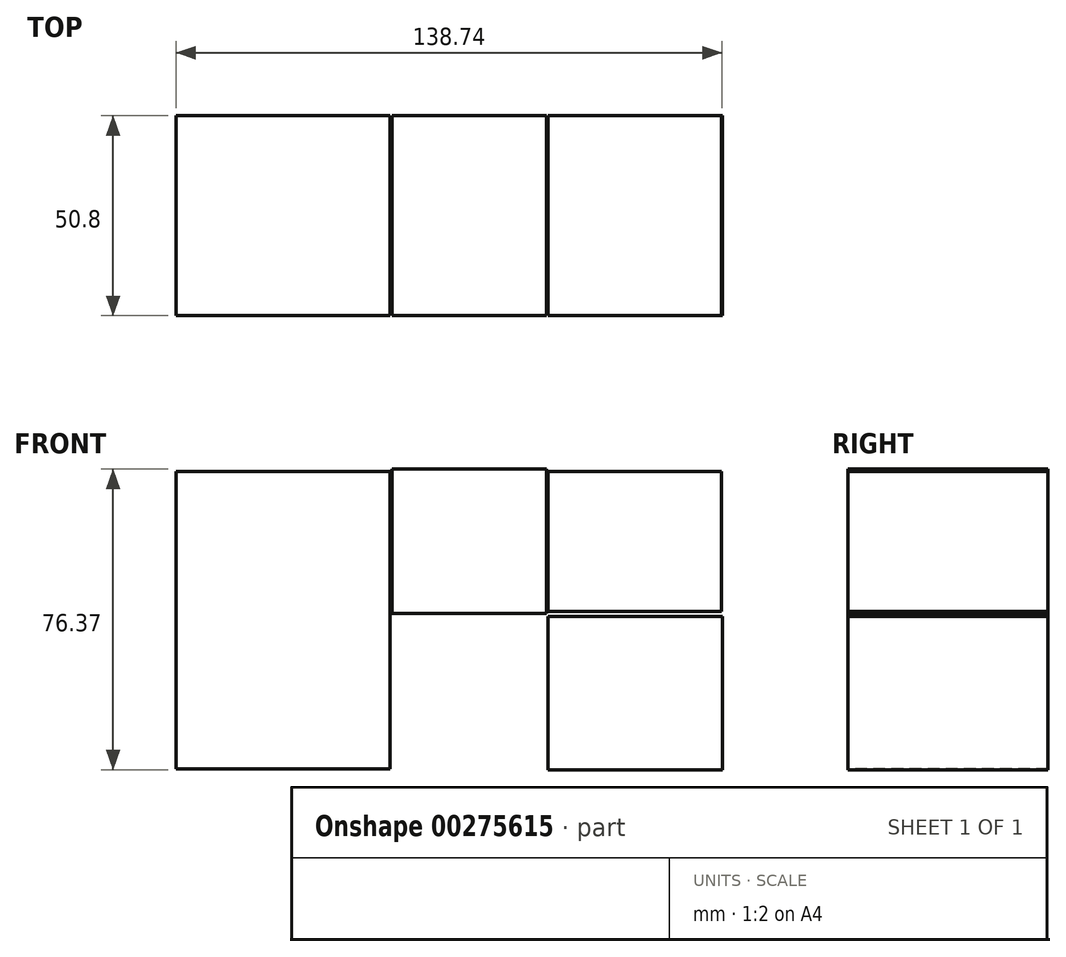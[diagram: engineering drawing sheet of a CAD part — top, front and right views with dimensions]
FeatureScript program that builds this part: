
annotation { "Feature Type Name" : "Feature", "Feature Type Description" : "" }
export const myFeature = defineFeature(function(context is Context, id is Id, definition is map)
    precondition{}
    {
        {
            var Q0;
            Q0=qCreatedBy(makeId("Front.planeOp"),FACE);
            var sketch = newSketch(context, id + "F0", { "sketchPlane" : qUnion([Q0])});
            skLineSegment(sketch, "E0.bottom", {"start": v(19.66, -0.53) * mm, "end": v(-19.66, -0.53) * mm});
            skLineSegment(sketch, "E0.top", {"start": v(19.66, 36.14) * mm, "end": v(-19.66, 36.14) * mm});
            skLineSegment(sketch, "E0.left", {"start": v(19.66, -0.53) * mm, "end": v(19.66, 36.14) * mm});
            skLineSegment(sketch, "E0.right", {"start": v(-19.66, -0.53) * mm, "end": v(-19.66, 36.14) * mm});
            skPoint(sketch, "E0.middle", {"position": v(0, 17.8) * mm});
            skLineSegment(sketch, "E1.bottom", {"start": v(64.1, 0) * mm, "end": v(20.06, 0) * mm});
            skLineSegment(sketch, "E1.top", {"start": v(64.1, 35.6) * mm, "end": v(20.06, 35.6) * mm});
            skLineSegment(sketch, "E1.left", {"start": v(64.1, 0) * mm, "end": v(64.1, 35.6) * mm});
            skLineSegment(sketch, "E1.right", {"start": v(20.06, 0) * mm, "end": v(20.06, 35.6) * mm});
            skPoint(sketch, "E1.middle", {"position": v(42.08, 17.8) * mm});
            skPoint(sketch, "E1.middle.positionSnap0", {"position": v(19.66, 17.8) * mm});
            skPoint(sketch, "E1.centerSnap0", {"position": v(19.66, 17.8) * mm});
            skLineSegment(sketch, "E2.bottom", {"start": v(-20.1, 0) * mm, "end": v(-74.46, 0) * mm});
            skLineSegment(sketch, "E2.top", {"start": v(-20.1, 35.6) * mm, "end": v(-74.46, 35.6) * mm});
            skLineSegment(sketch, "E2.left", {"start": v(-20.1, 0) * mm, "end": v(-20.1, 35.6) * mm});
            skLineSegment(sketch, "E2.right", {"start": v(-74.46, 0) * mm, "end": v(-74.46, 35.6) * mm});
            skPoint(sketch, "E2.middle", {"position": v(-47.28, 17.8) * mm});
            skLineSegment(sketch, "E3.bottom", {"start": v(-20.1, -40.04) * mm, "end": v(-74.46, -40.04) * mm});
            skLineSegment(sketch, "E3.left", {"start": v(-20.1, -40.04) * mm, "end": v(-20.1, 0) * mm});
            skLineSegment(sketch, "E3.right", {"start": v(-74.46, -40.04) * mm, "end": v(-74.46, 0) * mm});
            skPoint(sketch, "E3.middle", {"position": v(-47.28, -20.02) * mm});
            skPoint(sketch, "E3.middle.positionSnap0", {"position": v(-47.28, 0) * mm});
            skPoint(sketch, "E3.centerSnap0", {"position": v(-47.28, 0) * mm});
            skLineSegment(sketch, "E4.bottom", {"start": v(64.28, -40.23) * mm, "end": v(20.07, -40.23) * mm});
            skLineSegment(sketch, "E4.top", {"start": v(64.28, -1.22) * mm, "end": v(20.07, -1.22) * mm});
            skLineSegment(sketch, "E4.left", {"start": v(64.28, -40.23) * mm, "end": v(64.28, -1.22) * mm});
            skLineSegment(sketch, "E4.right", {"start": v(20.07, -40.23) * mm, "end": v(20.07, -1.22) * mm});
            skPoint(sketch, "E4.middle", {"position": v(42.18, -20.73) * mm});
            skSolve(sketch);
        }
        {
            var Q0;
            Q0=makeQuery(id+"F0.imprint","IMPRINT",FACE,{"disambiguationData":[TD([[makeQuery(id+"F0.imprint","IMPRINT",EDGE,{"derivedFrom":sQuery(id+"F0.wireOp",EDGE,"E2.top")}),1.0]])]});
            var Q1;
            Q1=makeQuery(id+"F0.imprint","IMPRINT",FACE,{"disambiguationData":[TD([[makeQuery(id+"F0.imprint","IMPRINT",EDGE,{"derivedFrom":sQuery(id+"F0.wireOp",EDGE,"E1.bottom")}),-1.0]])]});
            var Q2;
            Q2=makeQuery(id+"F0.imprint","IMPRINT",FACE,{"disambiguationData":[TD([[makeQuery(id+"F0.imprint","IMPRINT",EDGE,{"derivedFrom":sQuery(id+"F0.wireOp",EDGE,"E4.bottom")}),-1.0]])]});
            var Q3;
            Q3=makeQuery(id+"F0.imprint","IMPRINT",FACE,{"disambiguationData":[TD([[makeQuery(id+"F0.imprint","IMPRINT",EDGE,{"derivedFrom":sQuery(id+"F0.wireOp",EDGE,"E3.bottom")}),-1.0]])]});
            var Q4;
            Q4=makeQuery(id+"F0.imprint","IMPRINT",FACE,{"disambiguationData":[TD([[makeQuery(id+"F0.imprint","IMPRINT",EDGE,{"derivedFrom":sQuery(id+"F0.wireOp",EDGE,"E0.bottom")}),-1.0]])]});
            extrude(context, id + "F1", {"entities" : qUnion([Q0, Q1, Q2, Q3, Q4]), "oppositeDirection" : true, "depth" : 50.8 * mm});
        }
    });
